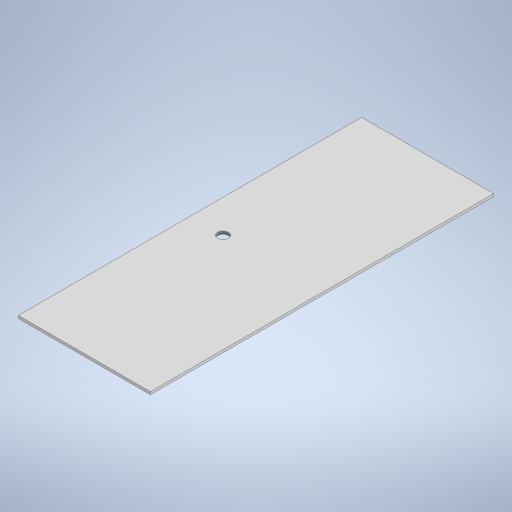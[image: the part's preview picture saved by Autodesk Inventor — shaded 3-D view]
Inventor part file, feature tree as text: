
AUTODESK INVENTOR PART (.ipt)
format: ipt  version: 2023 (Build 270158000, 158)  size: 215,040 bytes
history: native  units: mm
features: other x1, extrude x1, sketch x1
ambient origin geometry x8: Origin, YZ Plane, XZ Plane, XY Plane, X Axis, Y Axis, Z Axis, Center Point
bodies: Body1 (feature_tree)
feature tree (3):
  other  "Твердое тело1"
  extrude  "Выдавливание1"  Depth=200.0mm
  sketch  "Эскиз1"
